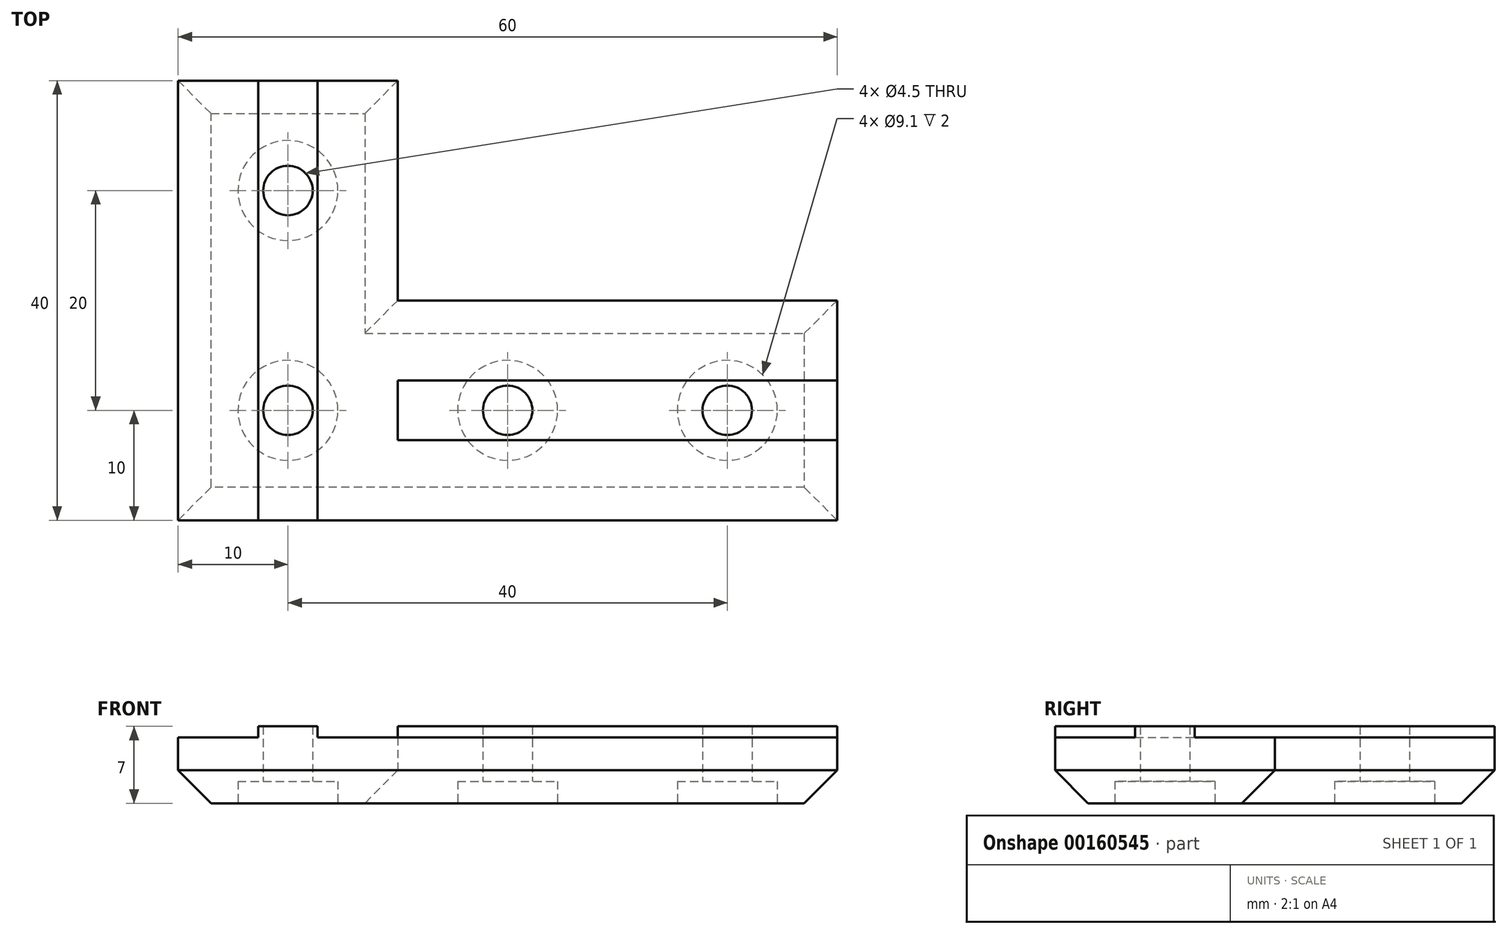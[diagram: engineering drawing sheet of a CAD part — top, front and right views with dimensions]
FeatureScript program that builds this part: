
annotation { "Feature Type Name" : "Feature", "Feature Type Description" : "" }
export const myFeature = defineFeature(function(context is Context, id is Id, definition is map)
    precondition{}
    {
        {
            var Q0;
            Q0=qCreatedBy(makeId("Top.planeOp"),FACE);
            var sketch = newSketch(context, id + "F0", { "sketchPlane" : qUnion([Q0])});
            skLineSegment(sketch, "E0", {"start": v(0, 0) * mm, "end": v(0, 40) * mm});
            skLineSegment(sketch, "E1", {"start": v(0, 40) * mm, "end": v(20, 40) * mm});
            skLineSegment(sketch, "E2", {"start": v(20, 40) * mm, "end": v(20, 20) * mm});
            skLineSegment(sketch, "E3", {"start": v(20, 20) * mm, "end": v(60, 20) * mm});
            skLineSegment(sketch, "E4", {"start": v(60, 20) * mm, "end": v(60, 0) * mm});
            skLineSegment(sketch, "E5", {"start": v(60, 0) * mm, "end": v(0, 0) * mm});
            skSolve(sketch);
        }
        {
            var Q0;
            Q0=qSketchRegion(id+"F0",true);
            extrude(context, id + "F1", {"entities" : qUnion([Q0]), "depth" : 6 * mm});
        }
        {
            var Q0;
            Q0=makeQuery(id+"F1.opExtrude","CAP_FACE",FACE,{"disambiguationData":[OSD([sQuery(id+"F0.wireOp",EDGE,"E0"),sQuery(id+"F0.wireOp",EDGE,"E1"),sQuery(id+"F0.wireOp",EDGE,"E2"),sQuery(id+"F0.wireOp",EDGE,"E3"),sQuery(id+"F0.wireOp",EDGE,"E4"),sQuery(id+"F0.wireOp",EDGE,"E5")])],"isStart":false});
            var sketch = newSketch(context, id + "F2", { "sketchPlane" : qUnion([Q0])});
            skLineSegment(sketch, "E6", {"start": v(7.3, 40) * mm, "end": v(12.71, 40) * mm});
            skLineSegment(sketch, "E7", {"start": v(12.71, 40) * mm, "end": v(12.71, 0) * mm});
            skLineSegment(sketch, "E8", {"start": v(12.71, 0) * mm, "end": v(10, 0) * mm});
            skPoint(sketch, "E8.endSnap0", {"position": v(10, 40) * mm});
            skLineSegment(sketch, "E9", {"start": v(10, 0) * mm, "end": v(7.3, 0) * mm});
            skLineSegment(sketch, "E10", {"start": v(7.3, 0) * mm, "end": v(7.3, 40) * mm});
            skLineSegment(sketch, "E11", {"start": v(60, 12.7) * mm, "end": v(60, 7.3) * mm});
            skLineSegment(sketch, "E12", {"start": v(60, 7.3) * mm, "end": v(20, 7.3) * mm});
            skLineSegment(sketch, "E13", {"start": v(20, 7.3) * mm, "end": v(20, 10) * mm});
            skPoint(sketch, "E13.endSnap0", {"position": v(60, 10) * mm});
            skLineSegment(sketch, "E14", {"start": v(20, 10) * mm, "end": v(20, 12.71) * mm});
            skLineSegment(sketch, "E15", {"start": v(20, 12.71) * mm, "end": v(60, 12.71) * mm});
            skSolve(sketch);
        }
        {
            var Q0;
            Q0=qSketchRegion(id+"F2",true);
            extrude(context, id + "F3", {"entities" : qUnion([Q0]), "operationType" : NewBodyOperationType.ADD, "flatOperationType" : FlatOperationType.REMOVE, "offsetDistance" : 25 * mm, "depth" : 1 * mm, "domain" : OperationDomain.MODEL});
        }
        {
            var Q0;
            Q0=makeQuery(id+"F1.opExtrude","CAP_FACE",FACE,{"disambiguationData":[OSD([sQuery(id+"F0.wireOp",EDGE,"E0"),sQuery(id+"F0.wireOp",EDGE,"E1"),sQuery(id+"F0.wireOp",EDGE,"E2"),sQuery(id+"F0.wireOp",EDGE,"E3"),sQuery(id+"F0.wireOp",EDGE,"E4"),sQuery(id+"F0.wireOp",EDGE,"E5")])],"isStart":true});
            var sketch = newSketch(context, id + "F4", { "sketchPlane" : qUnion([Q0])});
            skCircle(sketch, "E16", {"center": v(10, -10) * mm, "radius": 2.25 * mm});
            skCircle(sketch, "E17", {"center": v(50, -10) * mm, "radius": 2.25 * mm});
            skCircle(sketch, "E18", {"center": v(10, -30) * mm, "radius": 2.25 * mm});
            skCircle(sketch, "E19", {"center": v(30, -10) * mm, "radius": 2.25 * mm});
            skSolve(sketch);
        }
        {
            var Q0;
            Q0=qSketchRegion(id+"F4",true);
            extrude(context, id + "F5", {"entities" : qUnion([Q0]), "operationType" : NewBodyOperationType.REMOVE, "endBound" : BoundingType.THROUGH_ALL, "oppositeDirection" : true, "depth" : 25 * mm});
        }
        {
            var Q0;
            Q0=makeQuery(id+"F1.opExtrude","CAP_FACE",FACE,{"disambiguationData":[OSD([sQuery(id+"F0.wireOp",EDGE,"E0"),sQuery(id+"F0.wireOp",EDGE,"E1"),sQuery(id+"F0.wireOp",EDGE,"E2"),sQuery(id+"F0.wireOp",EDGE,"E3"),sQuery(id+"F0.wireOp",EDGE,"E4"),sQuery(id+"F0.wireOp",EDGE,"E5")])],"isStart":true});
            var sketch = newSketch(context, id + "F6", { "sketchPlane" : qUnion([Q0])});
            skCircle(sketch, "E20", {"center": v(10, -10) * mm, "radius": 4.55 * mm});
            skCircle(sketch, "E21", {"center": v(30, -10) * mm, "radius": 4.55 * mm});
            skCircle(sketch, "E22", {"center": v(50, -10) * mm, "radius": 4.55 * mm});
            skCircle(sketch, "E23", {"center": v(10, -30) * mm, "radius": 4.55 * mm});
            skSolve(sketch);
        }
        {
            var Q0;
            Q0=qSketchRegion(id+"F6",true);
            extrude(context, id + "F7", {"entities" : qUnion([Q0]), "operationType" : NewBodyOperationType.REMOVE, "oppositeDirection" : true, "depth" : 2 * mm});
        }
        {
            var Q0;
            Q0=makeQuery(id+"F1.opExtrude","CAP_EDGE",EDGE,{"disambiguationData":[OSD([sQuery(id+"F0.wireOp",EDGE,"E5")])],"isStart":true});
            var Q1;
            Q1=makeQuery(id+"F1.opExtrude","CAP_EDGE",EDGE,{"disambiguationData":[OSD([sQuery(id+"F0.wireOp",EDGE,"E0")])],"isStart":true});
            var Q2;
            Q2=makeQuery(id+"F1.opExtrude","CAP_EDGE",EDGE,{"disambiguationData":[OSD([sQuery(id+"F0.wireOp",EDGE,"E2")])],"isStart":true});
            var Q3;
            Q3=makeQuery(id+"F1.opExtrude","CAP_EDGE",EDGE,{"disambiguationData":[OSD([sQuery(id+"F0.wireOp",EDGE,"E3")])],"isStart":true});
            var Q4;
            Q4=makeQuery(id+"F1.opExtrude","CAP_EDGE",EDGE,{"disambiguationData":[OSD([sQuery(id+"F0.wireOp",EDGE,"E4")])],"isStart":true});
            var Q5;
            Q5=makeQuery(id+"F1.opExtrude","CAP_EDGE",EDGE,{"disambiguationData":[OSD([sQuery(id+"F0.wireOp",EDGE,"E1")])],"isStart":true});
            chamfer(context, id + "F8", {"entities" : qUnion([Q0, Q1, Q2, Q3, Q4, Q5]), "width" : 3 * mm, "tangentPropagation" : true});
        }
    });
